# Revit family: DLB070008
name_source: partatom
category: Appareils sanitaires
revit_build: Autodesk Revit 2015 (Build: 20140606_1530(x64)
units: mm (PartAtom-declared; Revit-internal decimal feet)

## types (1)
- DLB070008
    Category = WC
    Commentaires du type = Recessed squat WC pan
    Description = French manufacturer Delabie is a leader in the European sanitary ware market for non-domestic places. Water controls, solutions for disabled people, sanitary ware, for schools, leisure centres, offices, hospitals, airports…
    Fabricant = DELABIE
    Features  = Floor-recessed squat WC pan.
Bacteriostatic 304 stainless steel.
Stainless steel thickness 1.2mm.
One-piece pressed WC bowl, seam-free for easy maintenance and better hygiene.
Bowl shape suitable for male and female use.
Non-slip foot area.
Vertical waste outlet: Ø 100mm.
Flushing system with one 304 stainless steel spreader.
Weight: 6kg.
    Finish = Polished satin
    Grade = CE
    ManufacturerName = DELABIE
    ManufacturerURL = http://www.delabie.com
    Material = 304 stainless steel
    ModelNumber = 113610
    Modèle = SHA 700 squat WC pan
    Name = SHA 700 squat WC pan
    NominalHeight = 30 mm  [stored 0.0984252 ft]
    NominalLength = 700 mm  [stored 2.29659 ft]
    NominalWidth = 700 mm  [stored 2.29659 ft]
    ProductInformation = http://www.delabie.com
    Radius (In) = 17 mm
    Radius (Out) = 50 mm  [stored 0.164042 ft]
    SerialNumber = 3456330163637
    URL = http://www.delabie.com
    Version = v1
    WarrantyDescription = Any manufacturing defect
    WarrantyDurationUnit = 10 years
    Weight = 6kg

note: [stored X ft] marks values corroborated as IEEE doubles in the binary element streams (Revit-internal decimal feet)

## geometry (parser evidence)
native form markers: Blend x14, Sweep x8
no freeform markers — native parametric forms only
